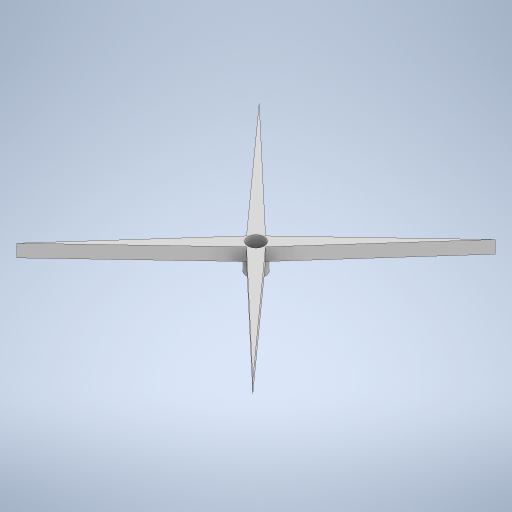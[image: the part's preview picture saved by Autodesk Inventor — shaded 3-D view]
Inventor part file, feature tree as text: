
AUTODESK INVENTOR PART (.ipt)
format: ipt  version: 2024.2 (Build 282272000, 272)  size: 257,024 bytes
history: native  units: mm
features: sketch x4, extrude x3
ambient origin geometry x8: Origin, YZ Plane, XZ Plane, XY Plane, X Axis, Y Axis, Z Axis, Center Point
bodies: Solid1 (feature_tree)
feature tree (7):
  extrude  "Extrusion1"  Depth=15.0mm
  extrude  "Extrusion2"  Depth=10.0mm TaperAngle=0.0deg
  sketch  "Sketch3"  dims[d6=0.0mm d7=0.0mm]
  extrude  "Extrusion3"  [1 undecoded]
  sketch  "Sketch1"  dims[d0=13.0mm d1=15.0mm]
  sketch  "Sketch2"  dims[d2=10.0mm d3=0.0mm d4=10.0mm d5=0.0mm]
  sketch  "Sketch4"
note: 1 required parameter value undecoded (feature->parameter linkage not recoverable at this tier; creation-order binding heuristic only, values carry confidence <= 0.55)
